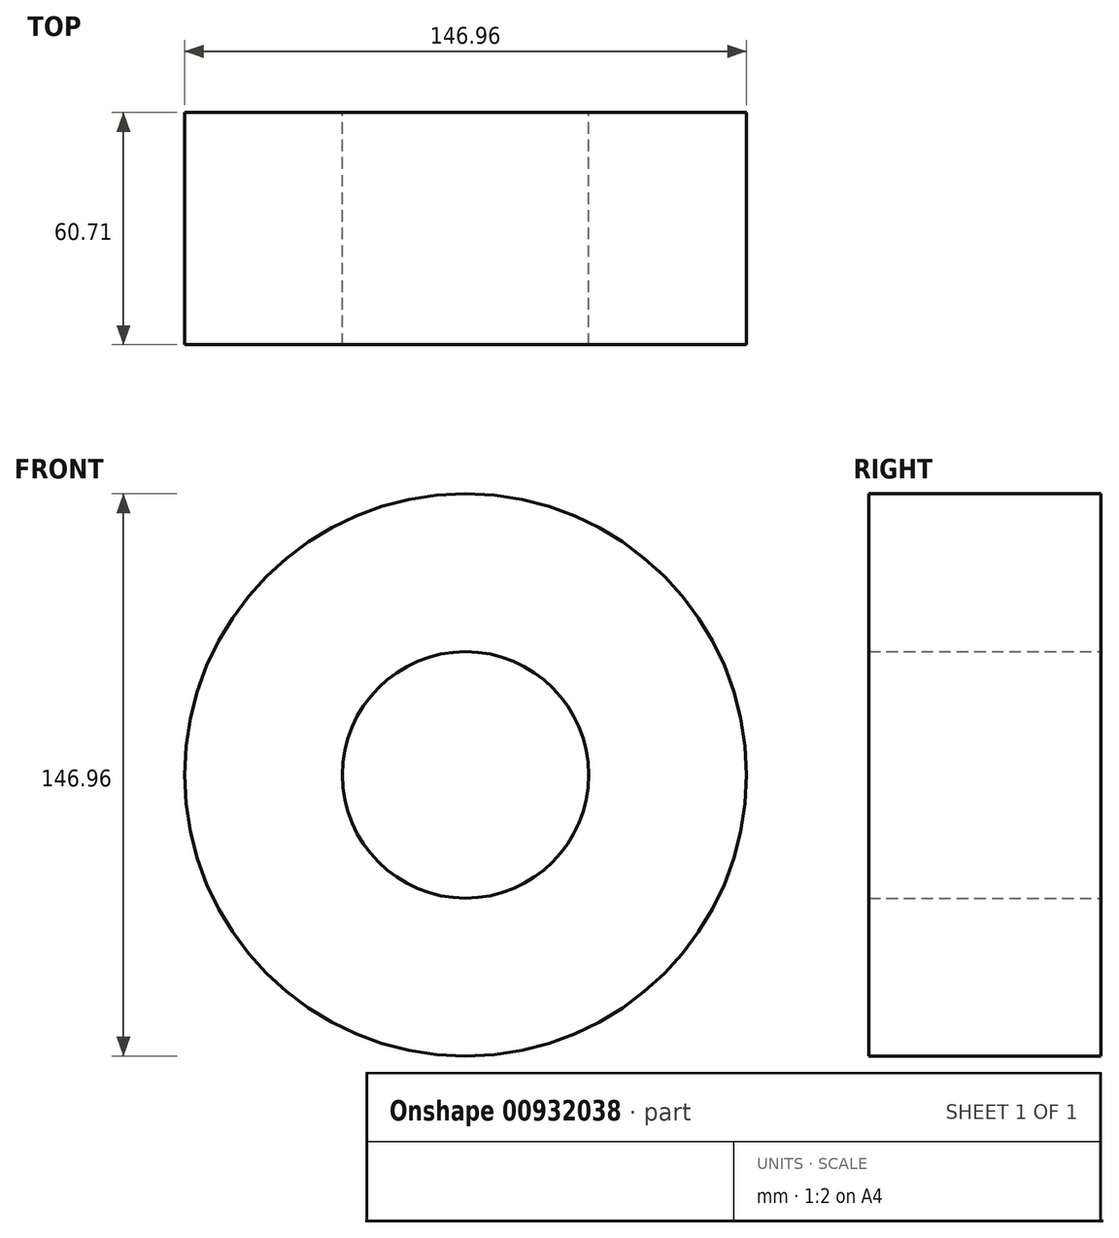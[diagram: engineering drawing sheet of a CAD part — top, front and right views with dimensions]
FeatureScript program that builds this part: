
annotation { "Feature Type Name" : "Feature", "Feature Type Description" : "" }
export const myFeature = defineFeature(function(context is Context, id is Id, definition is map)
    precondition{}
    {
        {
            var Q0;
            Q0=qCreatedBy(makeId("Front.planeOp"),FACE);
            var sketch = newSketch(context, id + "F0", { "sketchPlane" : qUnion([Q0])});
            skCircle(sketch, "E0", {"center": v(0, 0) * mm, "radius": 73.48 * mm});
            skSolve(sketch);
        }
        {
            var Q0;
            Q0=makeQuery(id+"F0.imprint","IMPRINT",FACE,{"disambiguationData":[TD([[makeQuery(id+"F0.imprint","IMPRINT",EDGE,{"derivedFrom":sQuery(id+"F0.wireOp",EDGE,"E0")}),1.0]])]});
            var sketch = newSketch(context, id + "F1", { "sketchPlane" : qUnion([Q0])});
            skCircle(sketch, "E1", {"center": v(0, 0) * mm, "radius": 32.22 * mm});
            skSolve(sketch);
        }
        {
            var Q0;
            Q0=makeQuery(id+"F1.imprint","IMPRINT",FACE,{"disambiguationData":[TD([[makeQuery(id+"F1.imprint","IMPRINT",EDGE,{"derivedFrom":sQuery(id+"F1.wireOp",EDGE,"E1")}),1.0]])]});
            var Q1;
            Q1=makeQuery(id+"F0.imprint","IMPRINT",FACE,{"disambiguationData":[TD([[makeQuery(id+"F0.imprint","IMPRINT",EDGE,{"derivedFrom":sQuery(id+"F0.wireOp",EDGE,"E0")}),1.0]])]});
            extrude(context, id + "F2", {"entities" : qUnion([Q0, Q1]), "depth" : 60.7 * mm, "offsetDistance" : 25.4 * mm});
        }
    });
